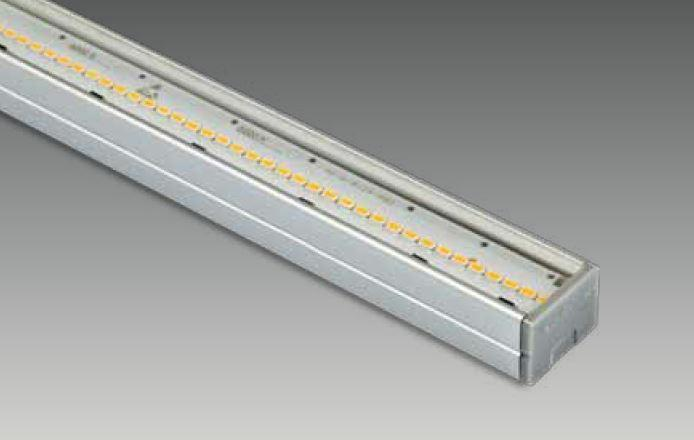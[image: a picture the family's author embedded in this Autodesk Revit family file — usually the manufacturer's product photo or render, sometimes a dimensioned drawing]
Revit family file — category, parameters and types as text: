
# Revit family: SD 1000 LIG-II
name_source: partatom
category: Lighting Fixtures
revit_build: Autodesk Revit 2016 (Build: 20150714_1515(x64)
units: mm (PartAtom-declared; Revit-internal decimal feet)

## family parameters
Cut with Voids When Loaded = No
Host = Face
Light Source = Yes
Part Type = Normal
Room Calculation Point = No
Round Connector Dimension = Use Diameter
Shared = No

## types (1)
- SDLIG.1000.20.30.110
    Color Filter = 16777215
    Default Elevation = 1219 mm
    Dimming Lamp Color Temperature Shift = <None>
    Emit Shape Visible in Rendering = Yes
    Emit from Rectangle Length = 15 mm  [stored 0.0492126 ft]
    Emit from Rectangle Width = 995 mm  [stored 3.26444 ft]
    Light Source Symbol Size = 610 mm
    Manufacturer = ARLIGHT
    Type Image = SD 1000 LIG.JPG
    Wattage Comments = 20

note: [stored X ft] marks values corroborated as IEEE doubles in the binary element streams (Revit-internal decimal feet)

## geometry (parser evidence)
native form markers: Sweep x3
no freeform markers — native parametric forms only
